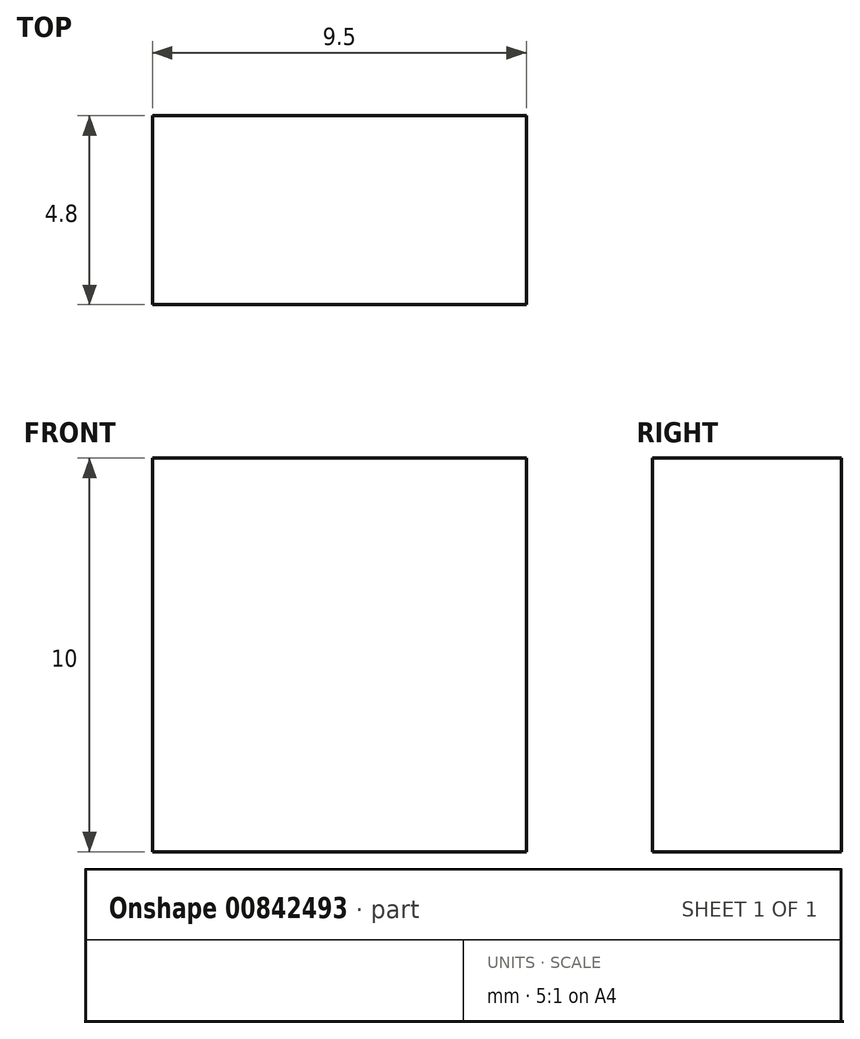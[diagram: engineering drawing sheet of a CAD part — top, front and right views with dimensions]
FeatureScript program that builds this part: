
annotation { "Feature Type Name" : "Feature", "Feature Type Description" : "" }
export const myFeature = defineFeature(function(context is Context, id is Id, definition is map)
    precondition{}
    {
        {
            var Q0;
            Q0=qCreatedBy(makeId("Top.planeOp"),FACE);
            var sketch = newSketch(context, id + "F0", { "sketchPlane" : qUnion([Q0])});
            skLineSegment(sketch, "E0.bottom", {"start": v(-9.5, 0) * mm, "end": v(0, 0) * mm});
            skLineSegment(sketch, "E0.top", {"start": v(-9.5, 4.8) * mm, "end": v(0, 4.8) * mm});
            skLineSegment(sketch, "E0.left", {"start": v(-9.5, 0) * mm, "end": v(-9.5, 4.8) * mm});
            skLineSegment(sketch, "E0.right", {"start": v(0, 0) * mm, "end": v(0, 4.8) * mm});
            skSolve(sketch);
        }
        {
            var Q0;
            Q0=qSketchRegion(id+"FRaLAdPDH5cZm7y_1",true);
            var Q1;
            Q1=qSketchRegion(id+"F0",true);
            extrude(context, id + "F1", {"entities" : qUnion([Q0, Q1]), "depth" : 10 * mm, "offsetDistance" : 25 * mm});
        }
    });
